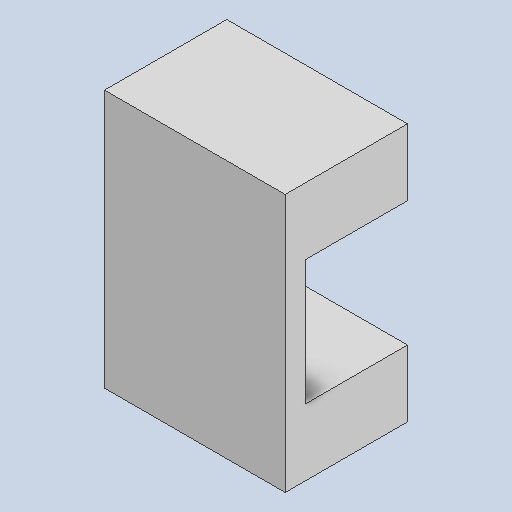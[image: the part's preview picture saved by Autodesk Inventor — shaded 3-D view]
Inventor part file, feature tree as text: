
AUTODESK INVENTOR PART (.ipt)
format: ipt  version: 2022 (Build 260153000, 153)  size: 149,504 bytes
history: native  units: mm
features: other x5, extrude x4, reference x4, sketch x3
ambient origin geometry x8: Origin, YZ Plane, XZ Plane, XY Plane, X Axis, Y Axis, Z Axis, Center Point
bodies: Solid1 (feature_tree)
feature tree (16):
  extrude  "Extrusion1"  Depth=0.3mm
  extrude  "Extrusion3"  Depth=0.3mm
  sketch  "Sketch5"  dims[d4=0.3mm d5=24.4mm d6=3.8mm d7=3.0mm d8=15.0mm d9=0.0mm d12=3.0mm d13=0.0mm d14=4.0mm d15=6.0mm d16=8.0mm d17=9.2mm d18=1.0mm d19=0.0mm d20=80.0mm d21=0.0mm]
  extrude  "Extrusion4"  Depth=24.4mm
  extrude  "Extrusion5"  Depth=3.8mm
  sketch  "Sketch1"  dims[d0=0.3mm d1=0.3mm]
  reference  "Reference1"
  reference  "Reference2"
  reference  "Reference3"
  reference  "Reference4"
  sketch  "Sketch4"  dims[d2=0.3mm d3=0.3mm]
  other  "<userpath>\OneDrive\Escritorio\Mini_Proyecto_Diseno\Diseno_18012\Modelo_MPD\Carril.iam"
  other  "Carril.iam"
  other  "Lateral_Carril:2"
  other  "Lateral_Carril:1"
  other  "Base_Carril:1"
